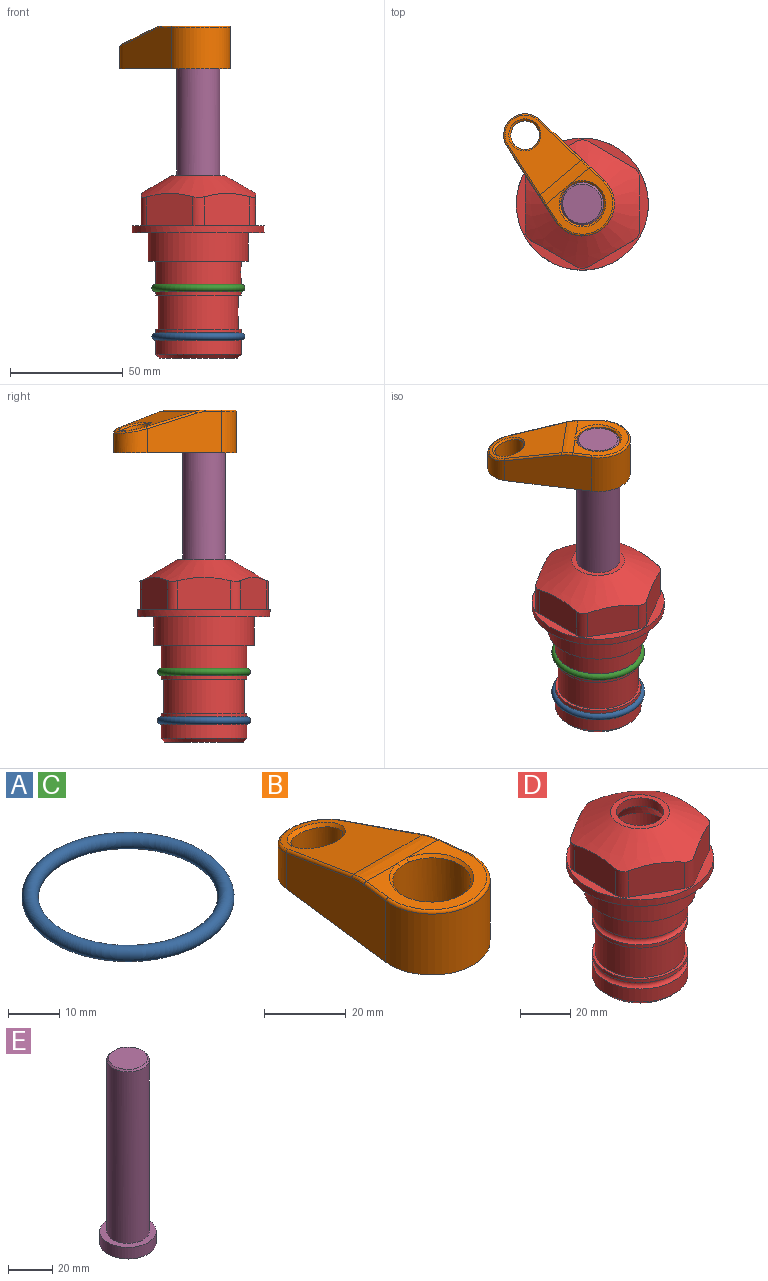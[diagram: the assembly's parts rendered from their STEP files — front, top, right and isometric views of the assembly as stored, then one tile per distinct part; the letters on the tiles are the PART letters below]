
ASSEMBLY  parts=5 mates=4
PART A: 1 faces, bbox 44.7x44.7x3.2 mm
  f0: torus R=19.05mm, axis (0,0,1), area 1193.9mm2
PART B: 31 faces, bbox 31.7x65.5x19.8 mm
  f0: plane 39.12x18.26mm, normal (0.99,0.12,0), area 612.2mm2, adj f1,f4,f7,f11,f13,f15
  f1: cylinder r=9.53mm len=18.91mm, axis (0,0,-1), area 296.1mm2, adj f0,f2,f7,f17
  f2: plane 39.12x18.26mm, normal (-0.99,0.12,0), area 612.2mm2, adj f1,f4,f7,f12,f14,f16
  f3: cylinder r=6.35mm len=12.7mm, axis (0,0,-1), area 362.4mm2, adj f7,f18
  f4: cylinder r=14.29mm len=28.58mm, axis (0,0,-1), area 882.2mm2, adj f0,f2,f7,f10
  f5: cylinder r=9.53mm len=19.05mm, axis (0,0,-1), area 1092.6mm2, adj f7,f19,f20
  f6: plane 26.99x23.69mm, normal (0,0,1), area 216.2mm2, adj f9,f10,f11,f12,f19
  f7: plane 63.5x28.58mm, normal (0,0,-1), area 661.8mm2, adj f0,f1,f2,f3,f4,f5,f22,f23
  f8: plane 33.52x23.6mm, normal (0,0.26,0.97), area 486mm2, adj f9,f15,f16,f17,f18
  f9: cylinder r=19.05mm len=24.72mm, axis (1,0,0), area 120.4mm2, adj f6,f8,f13,f14,f20
  f10: torus R=13.49mm, axis (0,0,1), area 59mm2, adj f4,f6,f11,f12
  f11: cylinder r=0.79mm len=8.67mm, axis (0.12,-0.99,0), area 10.8mm2, adj f0,f6,f10,f13
  f12: cylinder r=0.79mm len=8.67mm, axis (0.12,0.99,0), area 10.8mm2, adj f2,f6,f10,f14
  f13: bspline ~4.95x1.42mm, area 6.1mm2, adj f0,f9,f11,f15
  f14: bspline ~4.95x1.42mm, area 6.1mm2, adj f2,f9,f12,f16
  f15: cylinder r=0.79mm len=25.95mm, axis (0.12,-0.96,0.26), area 32.9mm2, adj f0,f8,f13,f17
  f16: cylinder r=0.79mm len=25.95mm, axis (0.12,0.96,-0.26), area 32.9mm2, adj f2,f8,f14,f17
  f17: bspline ~18.91x8.38mm, area 30mm2, adj f1,f8,f15,f16
  f18: bspline ~14.29x14.29mm, area 48.3mm2, adj f3,f8
  f19: cone r=9.53mm half-angle=45deg, axis (0,0,1), area 66.5mm2, adj f5,f6,f20
  f20: bspline ~3.22x0.96mm, area 3.5mm2, adj f5,f9,f19
  f21: plane 2.75x2.72mm, normal (0,0,-1), area 2.9mm2, adj f23,f25,f28
  f22: plane 23.05x15.88mm, normal (-0.99,-0.12,0), area 323.6mm2, adj f7,f25,f26,f27,f28,f29
  f23: plane 23.05x15.88mm, normal (0.99,-0.12,0), area 323.6mm2, adj f7,f21,f25,f27,f28,f30
  f24: cylinder r=9.53mm len=10.69mm, axis (0,0,-1), area 114.7mm2, adj f7,f27,f29,f30
  f25: cylinder r=12.7mm len=20.59mm, axis (0,0,-1), area 381.1mm2, adj f7,f21,f22,f23,f26,f28
  f26: plane 2.75x2.72mm, normal (0,0,-1), area 2.9mm2, adj f22,f25,f28
  f27: plane 19.72x18.37mm, normal (0,-0.26,-0.97), area 291.8mm2, adj f22,f23,f24,f28,f29,f30
  f28: cylinder r=15.88mm len=19.92mm, axis (1,0,0), area 54.8mm2, adj f21,f22,f23,f25,f26,f27
  f29: cylinder r=1.59mm len=11mm, axis (0,0,-1), area 34.7mm2, adj f7,f22,f24,f27
  f30: cylinder r=1.59mm len=11mm, axis (0,0,-1), area 34.7mm2, adj f7,f23,f24,f27
PART C: same geometry as A
PART D: 36 faces, bbox 58.7x58.7x81 mm
  f0: cylinder r=17.78mm len=35.56mm, axis (0,0,1), area 1670.8mm2, adj f23,f24,f31
  f1: cylinder r=19.05mm len=38.1mm, axis (0,0,1), area 1191.9mm2, adj f26,f27,f30
  f2: plane 58.66x58.66mm, normal (0,0,-1), area 1150.6mm2, adj f3,f28
  f3: cylinder r=29.33mm len=58.66mm, axis (0,0,-1), area 585.1mm2, adj f2,f4
  f4: plane 58.66x58.66mm, normal (0,0,1), area 475.9mm2, adj f3,f5,f6,f7,f8,f9,f10,f11
  f5: plane 20.32x14.34mm, normal (-0.5,0.87,0), area 324.4mm2, adj f4,f15,f16,f17
  f6: plane 20.32x14.34mm, normal (0.5,0.87,0), area 324.4mm2, adj f4,f14,f15,f17
  f7: plane 23.48x14.34mm, normal (1,0,0), area 324.4mm2, adj f4,f13,f14,f17
  f8: plane 20.32x14.34mm, normal (0.5,-0.87,0), area 324.4mm2, adj f4,f12,f13,f17
  f9: plane 20.32x14.34mm, normal (-0.5,-0.87,0), area 324.4mm2, adj f4,f11,f12,f17
  f10: plane 23.48x14.34mm, normal (-1,0,0), area 324.4mm2, adj f4,f11,f16,f17
  f11: cylinder r=5.08mm len=12.85mm, axis (0,0,-1), area 67.2mm2, adj f4,f9,f10,f17
  f12: cylinder r=5.08mm len=12.85mm, axis (0,0,-1), area 67.2mm2, adj f4,f8,f9,f17
  f13: cylinder r=5.08mm len=12.85mm, axis (0,0,-1), area 67.2mm2, adj f4,f7,f8,f17
  f14: cylinder r=5.08mm len=12.85mm, axis (0,0,-1), area 67.2mm2, adj f4,f6,f7,f17
  f15: cylinder r=5.08mm len=12.85mm, axis (0,0,-1), area 67.2mm2, adj f4,f5,f6,f17
  f16: cylinder r=5.08mm len=12.85mm, axis (0,0,-1), area 67.2mm2, adj f4,f5,f10,f17
  f17: cone r=11.73mm half-angle=60deg, axis (0,0,-1), area 2071.8mm2, adj f5,f6,f7,f8,f9,f10,f11,f12
  f18: plane 23.46x23.46mm, normal (0,0,1), area 147.4mm2, adj f17,f35
  f19: plane 34.93x34.93mm, normal (0,0,-1), area 958mm2, adj f29
  f20: cylinder r=19.05mm len=38.1mm, axis (0,0,1), area 760.1mm2, adj f21,f29
  f21: torus R=19.05mm, axis (0,0,1), area 565.3mm2, adj f20,f22
  f22: cylinder r=19.05mm len=38.1mm, axis (0,0,1), area 190mm2, adj f21,f23
  f23: plane 38.1x38.1mm, normal (0,0,1), area 146.9mm2, adj f0,f22
  f24: plane 38.1x38.1mm, normal (0,0,-1), area 146.9mm2, adj f0,f25
  f25: cylinder r=19.05mm len=38.1mm, axis (0,0,1), area 190mm2, adj f24,f26
  f26: torus R=19.05mm, axis (0,0,1), area 565.3mm2, adj f1,f25
  f27: plane 44.45x44.45mm, normal (0,0,-1), area 411.7mm2, adj f1,f28
  f28: cylinder r=22.23mm len=44.45mm, axis (0,0,1), area 1773.5mm2, adj f2,f27
  f29: cone r=19.05mm half-angle=45deg, axis (0,0,1), area 257.5mm2, adj f19,f20
  f30: cylinder r=3.17mm len=6.75mm, axis (-1,0,0), area 128mm2, adj f1,f33
  f31: cylinder r=3.17mm len=6.35mm, axis (-1,0,0), area 102.5mm2, adj f0,f33
  f32: plane 25.4x25.4mm, normal (0,0,1), area 506.7mm2, adj f33
  f33: cylinder r=12.7mm len=66.42mm, axis (0,0,-1), area 5236.2mm2, adj f30,f31,f32,f34
  f34: cone r=9.53mm half-angle=30deg, axis (0,0,-1), area 443.4mm2, adj f33,f35
  f35: cylinder r=9.53mm len=19.05mm, axis (0,0,-1), area 240.9mm2, adj f18,f34
PART E: 6 faces, bbox 25.4x25.4x101.6 mm
  f0: plane 17.46x17.46mm, normal (0,0,1), area 239.5mm2, adj f5
  f1: plane 25.4x25.4mm, normal (0,0,-1), area 506.7mm2, adj f2
  f2: cylinder r=12.7mm len=25.4mm, axis (0,0,1), area 506.7mm2, adj f1,f3
  f3: plane 25.4x25.4mm, normal (0,0,1), area 221.7mm2, adj f2,f4
  f4: cylinder r=9.53mm len=94.46mm, axis (0,0,1), area 5653mm2, adj f3,f5
  f5: cone r=8.73mm half-angle=45deg, axis (0,0,-1), area 64.4mm2, adj f0,f4
PLACE A t=(0,0,-21.59)mm
PLACE B rot(axis=(0,0,1),39.9deg) t=(0,0,28.35)mm
PLACE C at identity
PLACE D at identity fixed
PLACE E rot(axis=(0,0,1),39.9deg) t=(0,0,27.55)mm
MATE fastened E.f2 <-> B.f4  axis (0,0,1) through (0,0,91.05)mm
MATE fastened D.f0 <-> C.f0  axis (0,0,1) through (0,0,-24.51)mm
MATE fastened D.f0 <-> A.f0  axis (0,0,1) through (0,0,-46.1)mm
MATE cylindrical D.f0 <-> E.f2  axis (0,0,1) through (0,0,-50.55)mm
